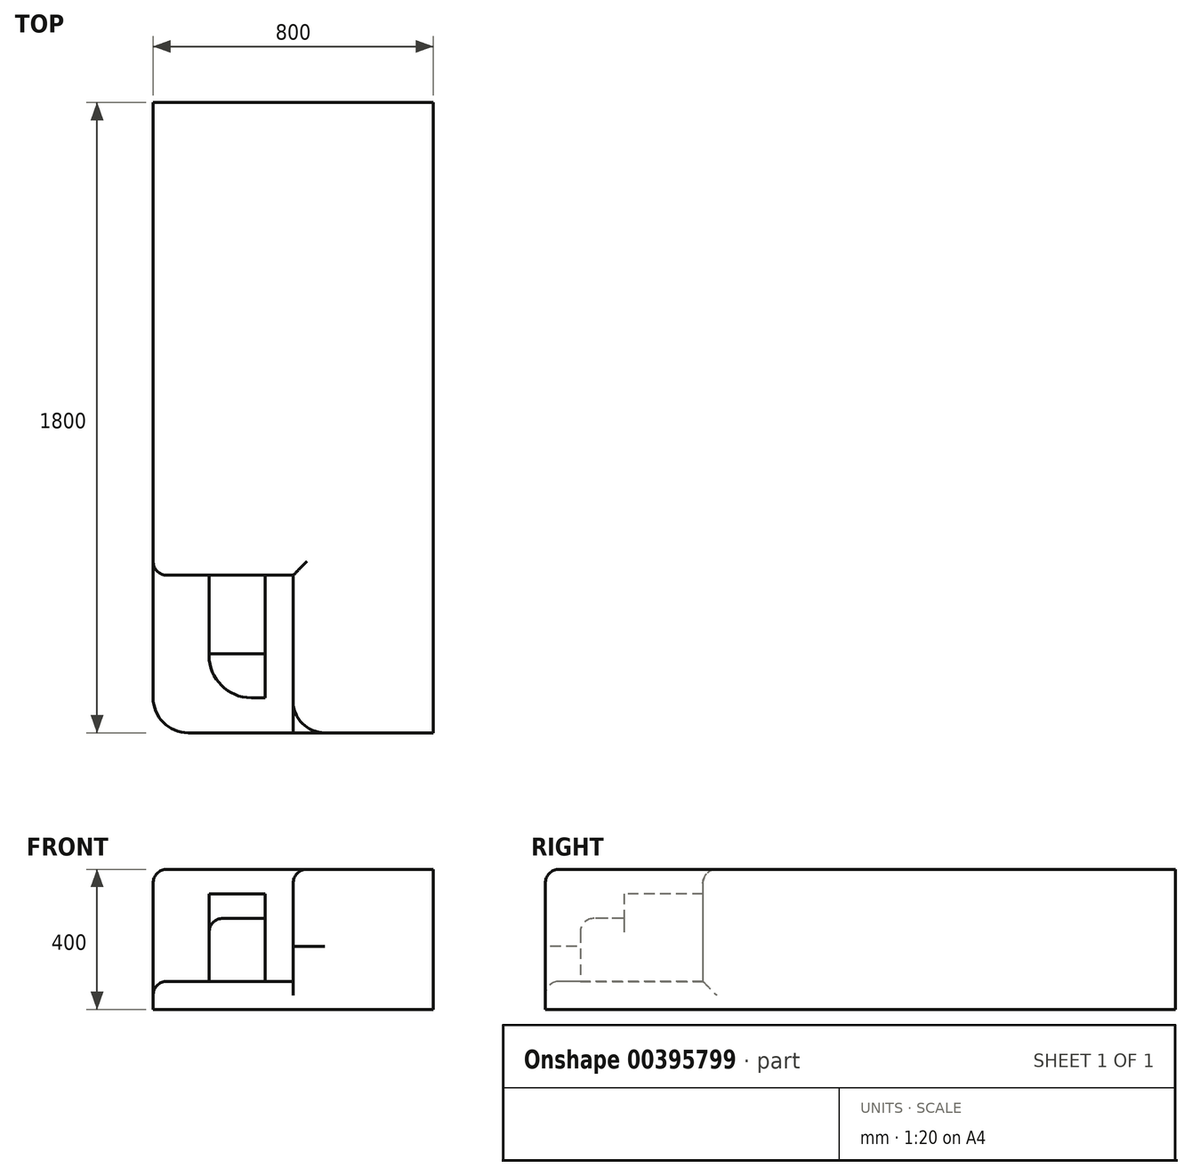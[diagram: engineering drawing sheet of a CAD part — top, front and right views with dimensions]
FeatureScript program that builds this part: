
annotation { "Feature Type Name" : "Feature", "Feature Type Description" : "" }
export const myFeature = defineFeature(function(context is Context, id is Id, definition is map)
    precondition{}
    {
        {
            var Q0;
            Q0=qCreatedBy(makeId("Top.planeOp"),FACE);
            var sketch = newSketch(context, id + "F0", { "sketchPlane" : qUnion([Q0])});
            skLineSegment(sketch, "E0.bottom", {"start": v(-300, -900) * mm, "end": v(400, -900) * mm});
            skLineSegment(sketch, "E0.top", {"start": v(-400, 900) * mm, "end": v(400, 900) * mm});
            skLineSegment(sketch, "E0.left", {"start": v(-400, -800) * mm, "end": v(-400, 900) * mm});
            skLineSegment(sketch, "E0.right", {"start": v(400, -900) * mm, "end": v(400, 900) * mm});
            skPoint(sketch, "E0.middle", {"position": v(0, 0) * mm});
            skPoint(sketch, "E1.visualSharp", {"position": v(-400, -900) * mm});
            skArc(sketch, "E1.filletArc", {"start": v(-400, -800) * mm, "mid": v(-370.71, -870.71) * mm, "end": v(-300, -900) * mm});
            skSolve(sketch);
        }
        {
            var Q0;
            Q0=makeQuery(id+"F0.imprint","IMPRINT",FACE,{"disambiguationData":[TD([[makeQuery(id+"F0.imprint","IMPRINT",EDGE,{"derivedFrom":sQuery(id+"F0.wireOp",EDGE,"E0.bottom")}),1.0]])]});
            extrude(context, id + "F1", {"entities" : qUnion([Q0]), "depth" : 80 * mm});
        }
        {
            var Q0;
            Q0=makeQuery(id+"F1.opExtrude","CAP_FACE",FACE,{"disambiguationData":[OSD([sQuery(id+"F0.wireOp",EDGE,"E0.bottom"),sQuery(id+"F0.wireOp",EDGE,"E0.top"),sQuery(id+"F0.wireOp",EDGE,"E0.left"),sQuery(id+"F0.wireOp",EDGE,"E0.right"),sQuery(id+"F0.wireOp",EDGE,"E1.filletArc")])],"isStart":false});
            var sketch = newSketch(context, id + "F2", { "sketchPlane" : qUnion([Q0])});
            skLineSegment(sketch, "E2.bottom", {"start": v(400, 900) * mm, "end": v(-400, 900) * mm});
            skLineSegment(sketch, "E2.top", {"start": v(400, -900) * mm, "end": v(90, -900) * mm});
            skLineSegment(sketch, "E2.left", {"start": v(400, 900) * mm, "end": v(400, -900) * mm});
            skLineSegment(sketch, "E2.right", {"start": v(-400, 900) * mm, "end": v(-400, -615) * mm});
            skPoint(sketch, "E2.middle", {"position": v(0, 0) * mm});
            skLineSegment(sketch, "E3.bottom", {"start": v(0, 0) * mm, "end": v(-400, 0) * mm});
            skLineSegment(sketch, "E3.top", {"start": v(0, -900) * mm, "end": v(-30, -900) * mm});
            skLineSegment(sketch, "E3.left", {"start": v(0, 0) * mm, "end": v(0, -900) * mm});
            skLineSegment(sketch, "E3.right", {"start": v(-400, 0) * mm, "end": v(-400, -410) * mm});
            skLineSegment(sketch, "E4.bottom", {"start": v(0, -450) * mm, "end": v(-80, -450) * mm});
            skLineSegment(sketch, "E4.top", {"start": v(0, -900) * mm, "end": v(-80, -900) * mm});
            skLineSegment(sketch, "E4.left", {"start": v(0, -450) * mm, "end": v(0, -810) * mm});
            skLineSegment(sketch, "E4.right", {"start": v(-80, -450) * mm, "end": v(-80, -850) * mm});
            skPoint(sketch, "E5.oppositeSnap0", {"position": v(-80, -675) * mm});
            skLineSegment(sketch, "E5.bottom", {"start": v(-80, -450) * mm, "end": v(-360, -450) * mm});
            skLineSegment(sketch, "E5.top", {"start": v(-80, -675) * mm, "end": v(-340, -675) * mm});
            skLineSegment(sketch, "E5.left", {"start": v(-80, -450) * mm, "end": v(-80, -675) * mm});
            skLineSegment(sketch, "E5.right", {"start": v(-400, -450) * mm, "end": v(-400, -670) * mm});
            skPoint(sketch, "E6.oppositeSnap0", {"position": v(-240, -675) * mm});
            skLineSegment(sketch, "E6.bottom", {"start": v(0, -450) * mm, "end": v(-240, -450) * mm});
            skLineSegment(sketch, "E6.top", {"start": v(0, -800) * mm, "end": v(-120, -800) * mm});
            skLineSegment(sketch, "E6.left", {"start": v(0, -450) * mm, "end": v(0, -800) * mm});
            skLineSegment(sketch, "E6.right", {"start": v(-240, -450) * mm, "end": v(-240, -680) * mm});
            skLineSegment(sketch, "E7.top", {"start": v(0, -675) * mm, "end": v(-170, -675) * mm});
            skLineSegment(sketch, "E7.left", {"start": v(0, -450) * mm, "end": v(0, -675) * mm});
            skLineSegment(sketch, "E7.right", {"start": v(-240, -450) * mm, "end": v(-240, -605) * mm});
            skPoint(sketch, "E8.newPointA", {"position": v(-400, -675) * mm});
            skArc(sketch, "E8.filletArc", {"start": v(-400, -615) * mm, "mid": v(-382.43, -657.43) * mm, "end": v(-340, -675) * mm});
            skPoint(sketch, "E9.visualSharp", {"position": v(-240, -800) * mm});
            skArc(sketch, "E9.filletArc", {"start": v(-240, -680) * mm, "mid": v(-204.85, -764.85) * mm, "end": v(-120, -800) * mm});
            skPoint(sketch, "E10.newPointA", {"position": v(-80, -900) * mm});
            skArc(sketch, "E10.filletArc", {"start": v(-80, -850) * mm, "mid": v(-65.36, -885.36) * mm, "end": v(-30, -900) * mm});
            skArc(sketch, "E11.filletArc", {"start": v(-240, -605) * mm, "mid": v(-219.5, -654.5) * mm, "end": v(-170, -675) * mm});
            skLineSegment(sketch, "E12", {"start": v(0, -900) * mm, "end": v(122.65, -900) * mm});
            skPoint(sketch, "E13.newPointA", {"position": v(-400, -900) * mm});
            skArc(sketch, "E13.filletArc", {"start": v(0, -810) * mm, "mid": v(26.36, -873.64) * mm, "end": v(90, -900) * mm});
            skArc(sketch, "E14.filletArc", {"start": v(-400, -410) * mm, "mid": v(-388.28, -438.28) * mm, "end": v(-360, -450) * mm});
            skSolve(sketch);
        }
        {
            var Q0;
            Q0=makeQuery(id+"F2.imprint","IMPRINT",FACE,{"disambiguationData":[TD([[makeQuery(id+"F2.imprint","IMPRINT",EDGE,{"derivedFrom":sQuery(id+"F2.wireOp",EDGE,"E2.bottom")}),-1.0]])]});
            var Q1;
            {var subQ1=sQuery(id+"F2.wireOp",EDGE,"E3.bottom");Q1=makeQuery(id+"F2.imprint","IMPRINT",FACE,{"disambiguationData":[TD([[makeQuery(id+"F2.imprint","IMPRINT",EDGE,{"derivedFrom":subQ1}),1.0]])]});}
            var Q2;
            {var subQ0=sQuery(id+"F2.wireOp",EDGE,"E5.left");Q2=makeQuery(id+"F2.imprint","IMPRINT",FACE,{"disambiguationData":[TD([[makeQuery(id+"F2.imprint","IMPRINT",EDGE,{"derivedFrom":subQ0}),1.0]])]});}
            var Q3;
            {var subQ2=sQuery(id+"F2.wireOp",EDGE,"E5.left");Q3=makeQuery(id+"F2.imprint","IMPRINT",FACE,{"disambiguationData":[TD([[makeQuery(id+"F2.imprint","IMPRINT",EDGE,{"derivedFrom":subQ2}),-1.0]])]});}
            extrude(context, id + "F3", {"entities" : qUnion([Q0, Q1, Q2, Q3]), "operationType" : NewBodyOperationType.ADD, "depth" : 320 * mm});
        }
        {
            var Q0;
            Q0=makeQuery(id+"F2.imprint","IMPRINT",FACE,{"disambiguationData":[TD([[makeQuery(id+"F2.imprint","IMPRINT",EDGE,{"derivedFrom":sQuery(id+"F2.wireOp",EDGE,"E5.bottom")}),1.0]])]});
            var Q1;
            {var subQ0=sQuery(id+"F2.wireOp",EDGE,"E11.filletArc");Q1=makeQuery(id+"F2.imprint","IMPRINT",FACE,{"disambiguationData":[TD([[makeQuery(id+"F2.imprint","IMPRINT",EDGE,{"derivedFrom":subQ0}),-1.0]])]});}
            extrude(context, id + "F4", {"entities" : qUnion([Q0, Q1]), "operationType" : NewBodyOperationType.ADD, "depth" : 250 * mm});
        }
        {
            var Q0;
            {var subQ0=sQuery(id+"F2.wireOp",EDGE,"E9.filletArc");Q0=makeQuery(id+"F2.imprint","IMPRINT",FACE,{"disambiguationData":[TD([[makeQuery(id+"F2.imprint","IMPRINT",EDGE,{"derivedFrom":subQ0}),1.0]])]});}
            var Q1;
            {var subQ5=sQuery(id+"F2.wireOp",EDGE,"E6.left");Q1=makeQuery(id+"F2.imprint","IMPRINT",FACE,{"disambiguationData":[TD([[makeQuery(id+"F2.imprint","IMPRINT",EDGE,{"derivedFrom":subQ5}),-1.0]])]});}
            var Q2;
            {var subQ0=sQuery(id+"F2.wireOp",EDGE,"E11.filletArc");Q2=makeQuery(id+"F2.imprint","IMPRINT",FACE,{"disambiguationData":[TD([[makeQuery(id+"F2.imprint","IMPRINT",EDGE,{"derivedFrom":subQ0}),-1.0]])]});}
            extrude(context, id + "F5", {"entities" : qUnion([Q0, Q1, Q2]), "operationType" : NewBodyOperationType.ADD, "depth" : 180 * mm});
        }
        {
            var Q0;
            {var subQ4=sQuery(id+"F2.wireOp",EDGE,"E4.left");Q0=makeQuery(id+"F2.imprint","IMPRINT",FACE,{"disambiguationData":[TD([[makeQuery(id+"F2.imprint","IMPRINT",EDGE,{"derivedFrom":subQ4}),-1.0]])]});}
            var Q1;
            {var subQ3=sQuery(id+"F2.wireOp",EDGE,"E13.filletArc");Q1=makeQuery(id+"F2.imprint","IMPRINT",FACE,{"disambiguationData":[TD([[makeQuery(id+"F2.imprint","IMPRINT",EDGE,{"derivedFrom":subQ3}),-1.0]])]});}
            extrude(context, id + "F6", {"entities" : qUnion([Q0, Q1]), "operationType" : NewBodyOperationType.ADD, "depth" : 100 * mm});
        }
        {
            var Q0;
            Q0=makeQuery(id+"F3.opExtrude","CAP_EDGE",EDGE,{"disambiguationData":[OSD([sQuery(id+"F2.wireOp",EDGE,"E11.filletArc")])],"isStart":false});
            var Q1;
            Q1=makeQuery(id+"F3.opExtrude","CAP_EDGE",EDGE,{"disambiguationData":[OSD([sQuery(id+"F2.wireOp",EDGE,"E13.filletArc")])],"isStart":false});
            var Q2;
            Q2=makeQuery(id+"F3.opExtrude","CAP_EDGE",EDGE,{"disambiguationData":[OSD([sQuery(id+"F2.wireOp",EDGE,"E5.bottom")])],"isStart":false});
            var Q3;
            Q3=makeQuery(id+"F4.opExtrude","CAP_EDGE",EDGE,{"disambiguationData":[OSD([sQuery(id+"F2.wireOp",EDGE,"E8.filletArc")])],"isStart":false});
            var Q4;
            Q4=makeQuery(id+"F5.opExtrude","CAP_EDGE",EDGE,{"disambiguationData":[OSD([sQuery(id+"F2.wireOp",EDGE,"E9.filletArc")])],"isStart":false});
            var Q5;
            Q5=makeQuery(id+"F6.opExtrude","CAP_EDGE",EDGE,{"disambiguationData":[OSD([sQuery(id+"F2.wireOp",EDGE,"E10.filletArc")])],"isStart":false});
            var Q6;
            Q6=makeQuery(id+"F1.opExtrude","CAP_EDGE",EDGE,{"disambiguationData":[OSD([sQuery(id+"F0.wireOp",EDGE,"E1.filletArc")])],"isStart":false});
            fillet(context, id + "F7", {"entities" : qUnion([Q0, Q1, Q2, Q3, Q4, Q5, Q6]), "radius" : 40 * mm, "tangentPropagation" : true, "allowEdgeOverflow" : false});
        }
    });
